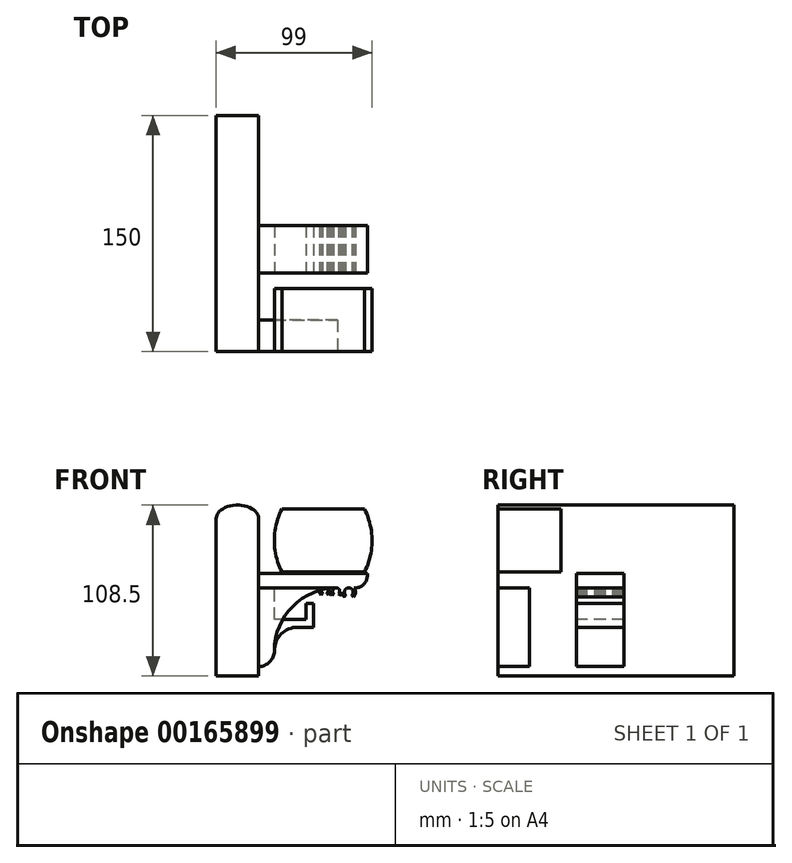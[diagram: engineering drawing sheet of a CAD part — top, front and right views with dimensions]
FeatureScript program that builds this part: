
annotation { "Feature Type Name" : "Feature", "Feature Type Description" : "" }
export const myFeature = defineFeature(function(context is Context, id is Id, definition is map)
    precondition{}
    {
        {
            var Q0;
            Q0=qCreatedBy(makeId("Front.planeOp"),FACE);
            var sketch = newSketch(context, id + "F0", { "sketchPlane" : qUnion([Q0])});
            skEllipticalArc(sketch, "E0", {});
            skLineSegment(sketch, "E1.bottom", {"start": v(0, 0) * mm, "end": v(13.5, 0) * mm, "construction": true});
            skLineSegment(sketch, "E1.top", {"start": v(-13.5, -100) * mm, "end": v(13.5, -100) * mm});
            skLineSegment(sketch, "E1.left", {"start": v(-13.5, 0) * mm, "end": v(-13.5, -100) * mm});
            skLineSegment(sketch, "E1.right", {"start": v(13.5, 0) * mm, "end": v(13.5, -100) * mm});
            skPoint(sketch, "E2", {"position": v(0, 8.5) * mm});
            const initialGuessF0  = {"E0": [0, 0, 1, 0, 0.0135, 0.0085, 0, 3.141592653589793]};
            skSetInitialGuess(sketch, initialGuessF0);
            skSolve(sketch);
        }
        {
            var Q0;
            Q0=qSketchRegion(id+"F0",true);
            extrude(context, id + "F1", {"entities" : qUnion([Q0]), "oppositeDirection" : true, "depth" : 150 * mm});
        }
        {
            var Q0;
            Q0=qCreatedBy(makeId("Front.planeOp"),FACE);
            var sketch = newSketch(context, id + "F2", { "sketchPlane" : qUnion([Q0])});
            skLineSegment(sketch, "E3", {"start": v(54.5, 6) * mm, "end": v(54.5, -34) * mm, "construction": true});
            skLineSegment(sketch, "E4", {"start": v(54.5, 6) * mm, "end": v(28.25, 6) * mm});
            skLineSegment(sketch, "E5", {"start": v(54.5, -34) * mm, "end": v(28.25, -34) * mm});
            skPoint(sketch, "E6", {"position": v(54.5, -14) * mm});
            skEllipticalArc(sketch, "E7", {});
            skPoint(sketch, "E8", {"position": v(23.5, -14) * mm});
            skPoint(sketch, "E9", {"position": v(28.25, 6) * mm});
            skEllipticalArc(sketch, "E10.MirrorCS", {});
            skLineSegment(sketch, "E11.MirrorCS", {"start": v(54.5, -34) * mm, "end": v(80.75, -34) * mm});
            skLineSegment(sketch, "E12.MirrorCS", {"start": v(54.5, 6) * mm, "end": v(80.75, 6) * mm});
            const initialGuessF2  = {"E7": [0.0545, -0.014, 0, 1, 0.037597341676323046, 0.031, 1.0098916143017092, 2.131701039288084], "E10.MirrorCS": [0.0545, -0.014, 0, 1, 0.037597341676323046, 0.031, 4.151484267891503, 5.273293692877877], "E10.MirrorCS": [0.0545, -0.014, 0, 1, 0.037597341676323046, 0.031, 4.151484267891503, 5.273293692877877]};
            skSetInitialGuess(sketch, initialGuessF2);
            skSolve(sketch);
        }
        {
            var Q0;
            Q0=qSketchRegion(id+"F2",true);
            extrude(context, id + "F3", {"entities" : qUnion([Q0]), "oppositeDirection" : true, "depth" : 40 * mm});
        }
        {
            var Q0;
            Q0=qCreatedBy(makeId("Front.planeOp"),FACE);
            var sketch = newSketch(context, id + "F4", { "sketchPlane" : qUnion([Q0])});
            skLineSegment(sketch, "E13.bottom", {"start": v(0, -44) * mm, "end": v(88, -44) * mm});
            skLineSegment(sketch, "E13.top", {"start": v(0, 18.5) * mm, "end": v(20.75, 18.5) * mm});
            skLineSegment(sketch, "E13.left", {"start": v(-23.5, -7.5) * mm, "end": v(-23.5, 0) * mm});
            skLineSegment(sketch, "E13.right", {"start": v(95.5, -36.5) * mm, "end": v(95.5, -1.5) * mm});
            skPoint(sketch, "E14", {"position": v(0, 8.5) * mm});
            skLineSegment(sketch, "E15", {"start": v(28.25, 6) * mm, "end": v(28.25, 11) * mm});
            skLineSegment(sketch, "E16", {"start": v(80.75, 6) * mm, "end": v(88, 6) * mm});
            skPoint(sketch, "E17", {"position": v(85.5, -14) * mm});
            skLineSegment(sketch, "E18", {"start": v(80.75, 6) * mm, "end": v(80.75, -34) * mm, "construction": true});
            skPoint(sketch, "E19", {"position": v(80.75, -14) * mm});
            skLineSegment(sketch, "E20", {"start": v(28.25, 6) * mm, "end": v(80.75, 6) * mm});
            skLineSegment(sketch, "E21", {"start": v(-16, -15) * mm, "end": v(0, -15) * mm});
            skLineSegment(sketch, "E22", {"start": v(0, -15) * mm, "end": v(0, -44) * mm});
            skPoint(sketch, "E23.visualSharp", {"position": v(-23.5, -15) * mm});
            skArc(sketch, "E23.filletArc", {"start": v(-23.5, -7.5) * mm, "mid": v(-21.3, -12.8) * mm, "end": v(-16, -15) * mm});
            skFitSpline(sketch, "E24.0", {"points": [v(23.36, -2.45) * mm, v(23.57, 0) * mm, v(23.36, 2.45) * mm, v(22.77, 4.78) * mm, v(21.86, 6.91) * mm, v(20.7, 8.82) * mm, v(19.36, 10.5) * mm, v(17.38, 12.45) * mm, v(14.68, 14.36) * mm, v(11.8, 15.76) * mm, v(9.39, 16.61) * mm, v(6.94, 17.3) * mm, v(4.44, 17.74) * mm, v(1.91, 17.96) * mm, v(0, 18.02) * mm, v(-1.91, 17.96) * mm, v(-4.44, 17.74) * mm, v(-6.94, 17.3) * mm, v(-9.39, 16.61) * mm, v(-11.8, 15.76) * mm, v(-14.68, 14.36) * mm, v(-17.38, 12.45) * mm, v(-19.36, 10.5) * mm, v(-20.7, 8.82) * mm, v(-21.86, 6.91) * mm, v(-22.77, 4.78) * mm, v(-23.36, 2.45) * mm, v(-23.57, 0) * mm, v(-23.36, -2.45) * mm, v(-22.77, -4.78) * mm, v(-21.86, -6.91) * mm, v(-20.7, -8.82) * mm, v(-19.36, -10.5) * mm, v(-17.38, -12.45) * mm, v(-14.68, -14.36) * mm, v(-11.8, -15.76) * mm, v(-9.39, -16.61) * mm, v(-6.94, -17.3) * mm, v(-4.44, -17.74) * mm, v(-1.91, -17.96) * mm, v(0, -18.02) * mm, v(1.91, -17.96) * mm, v(4.44, -17.74) * mm, v(6.94, -17.3) * mm, v(9.39, -16.61) * mm, v(11.8, -15.76) * mm, v(14.68, -14.36) * mm, v(17.38, -12.45) * mm, v(19.36, -10.5) * mm, v(20.7, -8.82) * mm, v(21.86, -6.91) * mm, v(22.77, -4.78) * mm, v(23.36, -2.45) * mm, v(23.57, 0) * mm, v(23.36, 2.45) * mm]});
            skPoint(sketch, "E25", {"position": v(0, 18.5) * mm});
            skPoint(sketch, "E26.visualSharp", {"position": v(28.25, 18.5) * mm});
            skArc(sketch, "E26.filletArc", {"start": v(28.25, 11) * mm, "mid": v(26.05, 16.3) * mm, "end": v(20.75, 18.5) * mm});
            skPoint(sketch, "E27.visualSharp", {"position": v(95.5, 6) * mm});
            skArc(sketch, "E27.filletArc", {"start": v(95.5, -1.5) * mm, "mid": v(93.3, 3.8) * mm, "end": v(88, 6) * mm});
            skPoint(sketch, "E28.visualSharp", {"position": v(95.5, -44) * mm});
            skArc(sketch, "E28.filletArc", {"start": v(88, -44) * mm, "mid": v(93.3, -41.8) * mm, "end": v(95.5, -36.5) * mm});
            skLineSegment(sketch, "E29.bottom", {"start": v(13.5, -84) * mm, "end": v(23.5, -84) * mm});
            skLineSegment(sketch, "E29.top", {"start": v(13.5, -44) * mm, "end": v(23.5, -44) * mm});
            skLineSegment(sketch, "E29.left", {"start": v(13.5, -84) * mm, "end": v(13.5, -44) * mm});
            skLineSegment(sketch, "E29.right", {"start": v(23.5, -84) * mm, "end": v(23.5, -44) * mm});
            skArc(sketch, "E30", {"start": v(23.5, -84) * mm, "mid": v(35.22, -55.72) * mm, "end": v(63.5, -44) * mm});
            skArc(sketch, "E31", {"start": v(23.5, -84) * mm, "mid": v(20.57, -91.07) * mm, "end": v(13.5, -94) * mm});
            skLineSegment(sketch, "E32", {"start": v(13.5, -94) * mm, "end": v(13.5, -84) * mm});
            skSolve(sketch);
        }
        {
            var Q0;
            Q0=qSketchRegion(id+"F4",true);
            extrude(context, id + "F5", {"entities" : qUnion([Q0]), "oppositeDirection" : true, "depth" : 20 * mm});
        }
        {
            var Q0;
            Q0=makeQuery(id+"F1.opExtrude","SWEPT_BODY",BODY,{"disambiguationData":[OSD([sQuery(id+"F0.wireOp",EDGE,"E0"),sQuery(id+"F0.wireOp",EDGE,"E1.top"),sQuery(id+"F0.wireOp",EDGE,"E1.left"),sQuery(id+"F0.wireOp",EDGE,"E1.right")])]});
            var Q1;
            Q1=makeQuery(id+"F3.opExtrude","SWEPT_BODY",BODY,{"disambiguationData":[OSD([sQuery(id+"F2.wireOp",EDGE,"E4"),sQuery(id+"F2.wireOp",EDGE,"E5"),sQuery(id+"F2.wireOp",EDGE,"E7"),sQuery(id+"F2.wireOp",EDGE,"E10.MirrorCS"),sQuery(id+"F2.wireOp",EDGE,"E11.MirrorCS"),sQuery(id+"F2.wireOp",EDGE,"E12.MirrorCS")])]});
            var Q2;
            Q2=makeQuery(id+"F5.opExtrude","SWEPT_BODY",BODY,{"disambiguationData":[OSD([sQuery(id+"F4.wireOp",EDGE,"E13.bottom"),sQuery(id+"F4.wireOp",EDGE,"E13.top"),sQuery(id+"F4.wireOp",EDGE,"E13.left"),sQuery(id+"F4.wireOp",EDGE,"E13.right"),sQuery(id+"F4.wireOp",EDGE,"E15"),sQuery(id+"F4.wireOp",EDGE,"E16"),sQuery(id+"F4.wireOp",EDGE,"E20"),sQuery(id+"F4.wireOp",EDGE,"E21"),sQuery(id+"F4.wireOp",EDGE,"E22"),sQuery(id+"F4.wireOp",EDGE,"E23.filletArc"),sQuery(id+"F4.wireOp",EDGE,"E24.0"),sQuery(id+"F4.wireOp",EDGE,"E26.filletArc"),sQuery(id+"F4.wireOp",EDGE,"E27.filletArc"),sQuery(id+"F4.wireOp",EDGE,"E28.filletArc")])]});
            booleanBodies(context, id + "F6", {"operationType" : BooleanOperationType.SUBTRACTION, "tools" : qUnion([Q0, Q1]), "targets" : qUnion([Q2]), "keepTools" : true});
        }
        {
            var Q0;
            Q0=qCreatedBy(makeId("Front.planeOp"),FACE);
            cPlane(context, id + "F7", {"entities" : qUnion([Q0]), "cplaneType" : CPlaneType.OFFSET, "offset" : 50 * mm, "oppositeDirection" : true, "width" : 150 * mm, "height" : 150 * mm});
        }
        {
            var Q0;
            Q0=qCreatedBy(id+"F7.planeOp",FACE);
            var sketch = newSketch(context, id + "F8", { "sketchPlane" : qUnion([Q0])});
            skLineSegment(sketch, "E33.bottom", {"start": v(13.5, -35) * mm, "end": v(82.5, -35) * mm});
            skLineSegment(sketch, "E33.top", {"start": v(0, 18.5) * mm, "end": v(16, 18.5) * mm});
            skLineSegment(sketch, "E33.left", {"start": v(-23.5, -7.5) * mm, "end": v(-23.5, 0) * mm});
            skPoint(sketch, "E34", {"position": v(0, 8.5) * mm});
            skLineSegment(sketch, "E35", {"start": v(23.5, -25) * mm, "end": v(23.5, 11) * mm});
            skPoint(sketch, "E36.visualSharp", {"position": v(-23.5, -15) * mm});
            skArc(sketch, "E36.filletArc", {"start": v(-23.5, -7.5) * mm, "mid": v(-21.3, -12.8) * mm, "end": v(-16, -15) * mm});
            skFitSpline(sketch, "E37.0", {"points": [v(23.45, -0.67) * mm, v(23.52, 1.8) * mm, v(23.18, 4.23) * mm, v(22.46, 6.52) * mm, v(21.43, 8.6) * mm, v(20.17, 10.44) * mm, v(18.73, 12.05) * mm, v(16.65, 13.88) * mm, v(13.85, 15.64) * mm, v(10.9, 16.87) * mm, v(8.44, 17.6) * mm, v(5.96, 18.14) * mm, v(3.44, 18.45) * mm, v(0.9, 18.53) * mm, v(-1.01, 18.48) * mm, v(-2.92, 18.32) * mm, v(-5.43, 17.95) * mm, v(-7.9, 17.37) * mm, v(-10.3, 16.55) * mm, v(-12.67, 15.57) * mm, v(-15.47, 14.02) * mm, v(-18.05, 11.96) * mm, v(-19.92, 9.9) * mm, v(-21.17, 8.15) * mm, v(-22.23, 6.18) * mm, v(-23.02, 4) * mm, v(-23.48, 1.64) * mm, v(-23.55, -0.82) * mm, v(-23.2, -3.25) * mm, v(-22.49, -5.54) * mm, v(-21.46, -7.63) * mm, v(-20.2, -9.47) * mm, v(-18.76, -11.07) * mm, v(-16.67, -12.9) * mm, v(-13.88, -14.67) * mm, v(-10.92, -15.9) * mm, v(-8.47, -16.62) * mm, v(-5.98, -17.17) * mm, v(-3.47, -17.47) * mm, v(-0.93, -17.55) * mm, v(0.98, -17.5) * mm, v(2.9, -17.34) * mm, v(5.4, -16.98) * mm, v(7.87, -16.4) * mm, v(10.28, -15.58) * mm, v(12.64, -14.6) * mm, v(15.44, -13.04) * mm, v(18.02, -10.98) * mm, v(19.9, -8.93) * mm, v(21.15, -7.18) * mm, v(22.2, -5.2) * mm, v(22.99, -3.02) * mm, v(23.45, -0.67) * mm, v(23.52, 1.8) * mm, v(23.18, 4.23) * mm]});
            skPoint(sketch, "E38.visualSharp", {"position": v(23.5, 18.5) * mm});
            skArc(sketch, "E38.filletArc", {"start": v(23.5, 11) * mm, "mid": v(21.3, 16.3) * mm, "end": v(16, 18.5) * mm});
            skLineSegment(sketch, "E39.bottom", {"start": v(13.5, -84) * mm, "end": v(23.5, -84) * mm});
            skLineSegment(sketch, "E39.top", {"start": v(13.5, -35) * mm, "end": v(23.5, -35) * mm});
            skLineSegment(sketch, "E39.left", {"start": v(13.5, -84) * mm, "end": v(13.5, -35) * mm});
            skLineSegment(sketch, "E39.right", {"start": v(23.5, -84) * mm, "end": v(23.5, -35) * mm});
            skArc(sketch, "E40", {"start": v(23.5, -84) * mm, "mid": v(20.57, -91.07) * mm, "end": v(13.5, -94) * mm});
            skLineSegment(sketch, "E41", {"start": v(13.5, -94) * mm, "end": v(13.5, -84) * mm});
            skPoint(sketch, "E42", {"position": v(28.25, 11) * mm});
            skLineSegment(sketch, "E43", {"start": v(23.5, -25) * mm, "end": v(77.5, -25) * mm});
            skLineSegment(sketch, "E44", {"start": v(77.5, -25) * mm, "end": v(77.5, 11) * mm});
            skArc(sketch, "E45", {"start": v(82.5, 6) * mm, "mid": v(81.04, 9.54) * mm, "end": v(77.5, 11) * mm});
            skLineSegment(sketch, "E46", {"start": v(82.5, 6) * mm, "end": v(82.5, -36.5) * mm});
            skLineSegment(sketch, "E47", {"start": v(13.5, -35) * mm, "end": v(13.5, 0) * mm});
            skLineSegment(sketch, "E48", {"start": v(-16, -15) * mm, "end": v(-13.5, -15) * mm});
            skLineSegment(sketch, "E49", {"start": v(-13.5, -15) * mm, "end": v(-13.5, 0) * mm});
            skEllipticalArc(sketch, "E50", {});
            skArc(sketch, "E51", {"start": v(38.5, -69) * mm, "mid": v(27.9, -73.4) * mm, "end": v(23.5, -84) * mm});
            skLineSegment(sketch, "E52", {"start": v(38.5, -69) * mm, "end": v(48.5, -69) * mm});
            skLineSegment(sketch, "E53", {"start": v(48.5, -69) * mm, "end": v(48.5, -54) * mm});
            skLineSegment(sketch, "E54", {"start": v(48.5, -54) * mm, "end": v(43.5, -54) * mm});
            skLineSegment(sketch, "E55", {"start": v(43.5, -54) * mm, "end": v(43.5, -64) * mm});
            skLineSegment(sketch, "E56", {"start": v(43.5, -64) * mm, "end": v(23.5, -64) * mm});
            skLineSegment(sketch, "E57", {"start": v(23.5, -64) * mm, "end": v(23.5, -44) * mm});
            skLineSegment(sketch, "E58", {"start": v(23.5, -44) * mm, "end": v(75, -44) * mm});
            skArc(sketch, "E59", {"start": v(75, -44) * mm, "mid": v(80.3, -41.8) * mm, "end": v(82.5, -36.5) * mm});
            skArc(sketch, "E60", {"start": v(72.7, -48.7) * mm, "mid": v(70.76, -44) * mm, "end": v(68.82, -48.7) * mm});
            skPoint(sketch, "E61", {"position": v(70.76, -44) * mm});
            skArc(sketch, "E62", {"start": v(73.76, -49.76) * mm, "mid": v(75, -46.92) * mm, "end": v(74, -44) * mm});
            skLineSegment(sketch, "E63", {"start": v(70.76, -46.75) * mm, "end": v(70.76, -44) * mm, "construction": true});
            skLineSegment(sketch, "E64", {"start": v(72.7, -48.7) * mm, "end": v(73.76, -49.76) * mm});
            skLineSegment(sketch, "E65.MirrorCS", {"start": v(68.82, -48.7) * mm, "end": v(67.75, -49.76) * mm});
            skArc(sketch, "E66.trimOffspring", {"start": v(67.52, -44) * mm, "mid": v(66.51, -46.92) * mm, "end": v(67.75, -49.76) * mm});
            skArc(sketch, "E67", {"start": v(64.37, -47.84) * mm, "mid": v(62.78, -44) * mm, "end": v(61.18, -47.84) * mm});
            skPoint(sketch, "E68", {"position": v(62.78, -44) * mm});
            skArc(sketch, "E69", {"start": v(65.43, -48.9) * mm, "mid": v(66.52, -46.52) * mm, "end": v(65.78, -44) * mm});
            skLineSegment(sketch, "E70", {"start": v(62.78, -46.25) * mm, "end": v(62.78, -44) * mm, "construction": true});
            skLineSegment(sketch, "E71", {"start": v(64.37, -47.84) * mm, "end": v(65.43, -48.9) * mm});
            skLineSegment(sketch, "E72.MirrorCS", {"start": v(61.18, -47.84) * mm, "end": v(60.12, -48.9) * mm});
            skArc(sketch, "E73.trimOffspring", {"start": v(59.78, -44) * mm, "mid": v(59.03, -46.52) * mm, "end": v(60.12, -48.9) * mm});
            skArc(sketch, "E74", {"start": v(56.94, -47.41) * mm, "mid": v(55.53, -44) * mm, "end": v(54.12, -47.41) * mm});
            skPoint(sketch, "E75", {"position": v(55.53, -44) * mm});
            skArc(sketch, "E76", {"start": v(58, -48.47) * mm, "mid": v(59.02, -46.3) * mm, "end": v(58.4, -44) * mm});
            skLineSegment(sketch, "E77", {"start": v(55.53, -46) * mm, "end": v(55.53, -44) * mm, "construction": true});
            skLineSegment(sketch, "E78", {"start": v(56.94, -47.41) * mm, "end": v(58, -48.47) * mm});
            skLineSegment(sketch, "E79.MirrorCS", {"start": v(54.12, -47.41) * mm, "end": v(53.05, -48.47) * mm});
            skArc(sketch, "E80.trimOffspring", {"start": v(52.66, -44) * mm, "mid": v(52.04, -46.3) * mm, "end": v(53.05, -48.47) * mm});
            skLineSegment(sketch, "E81", {"start": v(62.78, -46.25) * mm, "end": v(55.53, -46) * mm, "construction": true});
            skPoint(sketch, "E82", {"position": v(59.03, -46.12) * mm});
            skLineSegment(sketch, "E83", {"start": v(62.78, -46.25) * mm, "end": v(70.76, -46.75) * mm, "construction": true});
            skPoint(sketch, "E84", {"position": v(66.52, -46.48) * mm});
            const initialGuessF8  = {"E50": [0, 0, 1, 0, 0.0135, 0.0085, 0, 3.141592653589793]};
            skSetInitialGuess(sketch, initialGuessF8);
            skSolve(sketch);
        }
        {
            var Q0;
            Q0=qSketchRegion(id+"F8",true);
            extrude(context, id + "F9", {"entities" : qUnion([Q0]), "oppositeDirection" : true, "depth" : 30 * mm});
        }
    });
